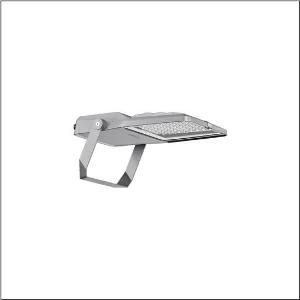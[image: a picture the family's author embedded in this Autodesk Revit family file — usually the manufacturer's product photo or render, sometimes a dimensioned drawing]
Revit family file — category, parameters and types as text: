
# Revit family: floodlight_fl_21_iq_mini___pl52_5xa7771d4d1a_c00e
name_source: partatom
category: Lighting Fixtures
units: mm (PartAtom-declared; Revit-internal decimal feet)

## family parameters
Cut with Voids When Loaded = No
Host = Face
Light Source = No
Part Type = Normal
Room Calculation Point = No
Round Connector Dimension = Use Diameter
Shared = No

## types (1)
- --- (1 x LED, 18610 lm, 143 W, 4000K)
    Apparent Load = 143 VA
    CIE Flux Codes = 26 60 98 100 100
    Color Rendering = 70
    Color Temperature = 4000K
    Default Elevation = 1800 mm
    Description = Floodlight FL 21 iQ mini, floodlight, primary light control with lens, of PMMA, primary optical cover: protective disc, of toughened safety glass, transparent, light distribution: PL52, light emission: direct distribution, installation type: surface-mounted, LED, High Power LED, rated luminous flux: 18.610lm, luminous efficacy: 130lm/W, light colour: 740, colour temperature: 4000K, control: Auto-Match, Temp-Guard, Lumen-Switch, Night-Set, Smart-Wire, Light-Fading, Desk-Remote (wireless, voltage-free reading and setting of iQ features in the workshop via application-optimized NFC function/RFID function), optimised constant luminous flux control (CLO 2.0), with terminal, 6-pole, mains connection: 220..240V, AC, 50/60Hz, start of lifetime: 143W, end of service life: 152W, reduction: 61W, luminaire housing, of diecast aluminium, powder-coated, Siteco® metallic grey (DB 702S), corrosivity category C5 mid according to DIN EN ISO 12944, sealing non-destructively replaceable, mounting bracket, of steel, galvanised, powder-coated, Siteco® metallic grey (DB 702S), protection rating (complete): IP66, insulation class (complete): insulation class II (safety insulation), certification: CE, ENEC, VDE, protection symbol: D, impact resistance: IK08, permissible operating ambient temperature: -40..+40°C, permissible operating ambient temperature for outdoor applications: -40..+50°C, standard: DIN EN 12944, LABS conformity tested according to VDMA 24364:2018-05, packaging unit: 1 piece

Light Distribution: PL52
    Height = 70 mm
    Lamp = 1 x LED
    Lamp Light Flux = 18610 lm
    Lamp Power = 143 W
    Lamp count = 1
    Length = 485 mm
    Luminous efficacy = 130 lm/W
    Manufacturer = Siteco
    ModVariant = No
    Model = 5XA7771D4D1A
    Number of Poles = 1
    OnlyDefault = Yes
    Power Factor = 1
    Product Name = Floodlight FL 21 iQ mini | PL52
    Product group = floodlight | pylon annexe
    ProductGroupID = 6200
    Protection Class = Protection class II
    Protection Degree = IP 66
    RLX_Detail_Level = 1
    RLX_Emergency_Light_Flux = 0 lm
    RLX_Emergency_Type = 0
    RLX_Emergency_Type_DB = No
    RlxData = <blob elided: 96689 chars, md5=817ba3e8>
    Socket = socket
    Standby Power = 0 W
    System Light Flux = 18610 lm
    System Power = 143 W
    Type Comments = factory setting: luminous flux: 100 % | dim-lin: 254 | 730 mA
    Type Image = l_1006845.jpg
    URL = http://relux.com
    VarID = @adj_114091
    Voltage = 0 V
    Weight = 0.00 kg
    Width = 337 mm

## geometry (parser evidence)
native form markers: Blend x4, Sweep x13
no freeform markers — native parametric forms only
